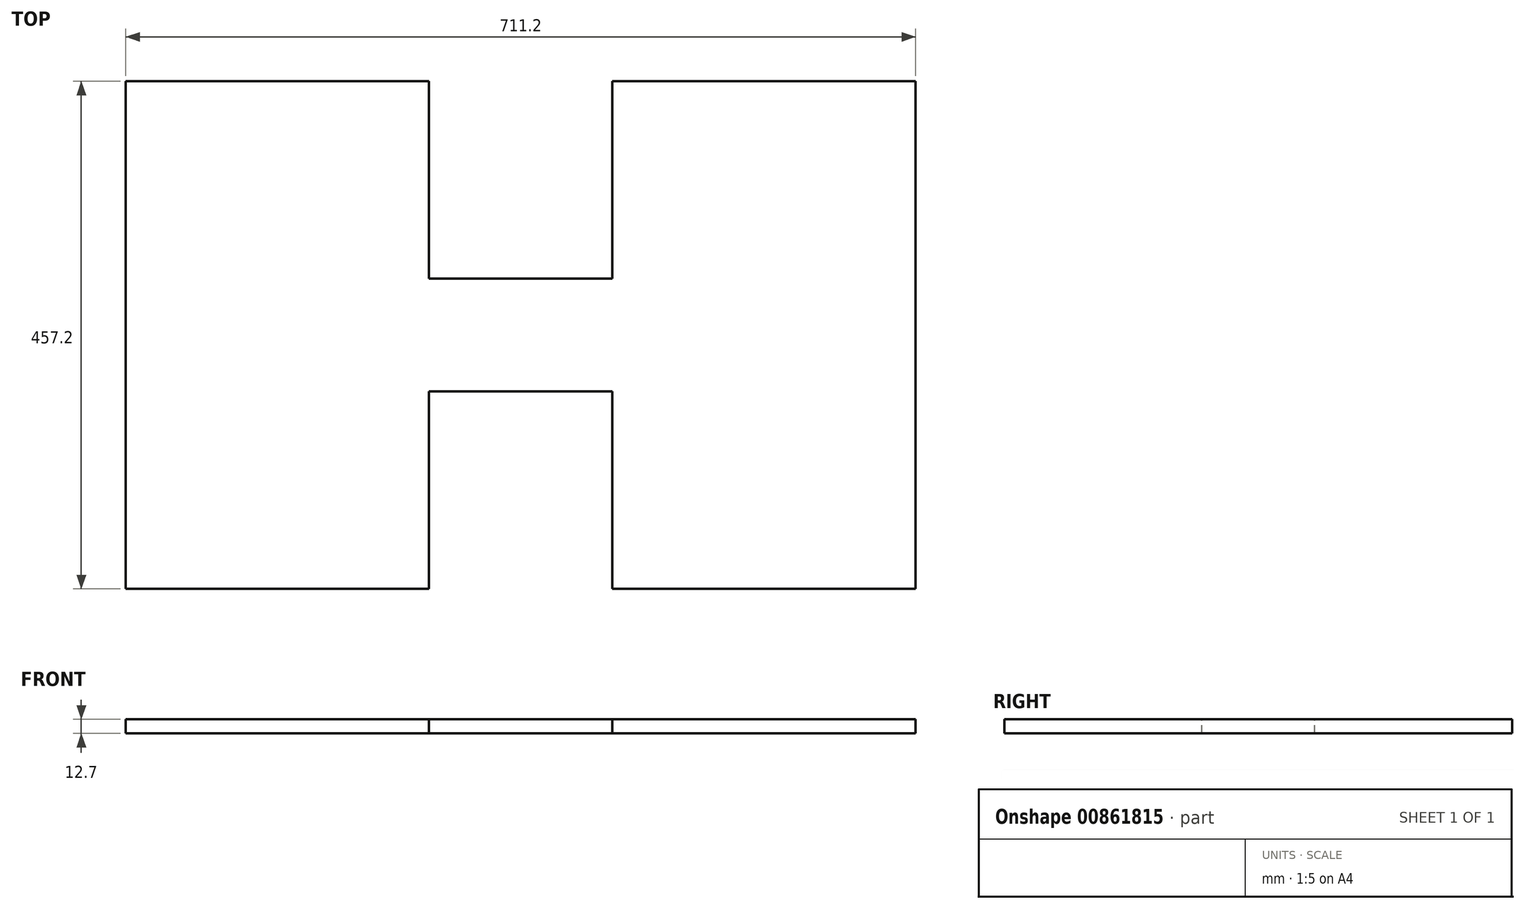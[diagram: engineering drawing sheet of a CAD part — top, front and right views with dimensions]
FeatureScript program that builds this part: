
annotation { "Feature Type Name" : "Feature", "Feature Type Description" : "" }
export const myFeature = defineFeature(function(context is Context, id is Id, definition is map)
    precondition{}
    {
        {
            var Q0;
            Q0=qCreatedBy(makeId("Top.planeOp"),FACE);
            var sketch = newSketch(context, id + "F0", { "sketchPlane" : qUnion([Q0])});
            skLineSegment(sketch, "E0.bottom", {"start": v(0, 0) * mm, "end": v(-711.2, 0) * mm});
            skLineSegment(sketch, "E0.top", {"start": v(0, 457.2) * mm, "end": v(-711.2, 457.2) * mm});
            skLineSegment(sketch, "E0.left", {"start": v(0, 0) * mm, "end": v(0, 457.2) * mm});
            skLineSegment(sketch, "E0.right", {"start": v(-711.2, 0) * mm, "end": v(-711.2, 457.2) * mm});
            skSolve(sketch);
        }
        {
            var Q0;
            Q0=makeQuery(id+"F0.imprint","IMPRINT",FACE,{"disambiguationData":[TD([[makeQuery(id+"F0.imprint","IMPRINT",EDGE,{"derivedFrom":sQuery(id+"F0.wireOp",EDGE,"E0.bottom")}),-1.0]])]});
            extrude(context, id + "F1", {"entities" : qUnion([Q0]), "depth" : 12.7 * mm, "offsetDistance" : 25.4 * mm});
        }
        {
            var Q0;
            Q0=makeQuery(id+"F1.opExtrude","CAP_FACE",FACE,{"disambiguationData":[OSD([sQuery(id+"F0.wireOp",EDGE,"E0.bottom"),sQuery(id+"F0.wireOp",EDGE,"E0.top"),sQuery(id+"F0.wireOp",EDGE,"E0.left"),sQuery(id+"F0.wireOp",EDGE,"E0.right")])],"isStart":false});
            var sketch = newSketch(context, id + "F2", { "sketchPlane" : qUnion([Q0])});
            skLineSegment(sketch, "E1.bottom", {"start": v(-273.05, 457.2) * mm, "end": v(-438.15, 457.2) * mm});
            skLineSegment(sketch, "E1.top", {"start": v(-273.05, 279.4) * mm, "end": v(-438.15, 279.4) * mm});
            skLineSegment(sketch, "E1.left", {"start": v(-273.05, 457.2) * mm, "end": v(-273.05, 279.4) * mm});
            skLineSegment(sketch, "E1.right", {"start": v(-438.15, 457.2) * mm, "end": v(-438.15, 279.4) * mm});
            skLineSegment(sketch, "E2.bottom", {"start": v(-438.15, 0) * mm, "end": v(-273.05, 0) * mm});
            skLineSegment(sketch, "E2.top", {"start": v(-438.15, 177.8) * mm, "end": v(-273.05, 177.8) * mm});
            skLineSegment(sketch, "E2.left", {"start": v(-438.15, 0) * mm, "end": v(-438.15, 177.8) * mm});
            skLineSegment(sketch, "E2.right", {"start": v(-273.05, 0) * mm, "end": v(-273.05, 177.8) * mm});
            skLineSegment(sketch, "E3", {"start": v(-273.05, 279.4) * mm, "end": v(-273.05, 177.8) * mm, "construction": true});
            skLineSegment(sketch, "E4", {"start": v(-438.15, 177.8) * mm, "end": v(-711.2, 177.8) * mm, "construction": true});
            skLineSegment(sketch, "E5", {"start": v(-273.05, 177.8) * mm, "end": v(0, 177.8) * mm, "construction": true});
            skSolve(sketch);
        }
        {
            var Q0;
            Q0=makeQuery(id+"F2.imprint","IMPRINT",FACE,{"disambiguationData":[TD([[makeQuery(id+"F2.imprint","IMPRINT",EDGE,{"derivedFrom":sQuery(id+"F2.wireOp",EDGE,"E1.bottom")}),1.0]])]});
            var Q1;
            Q1=makeQuery(id+"F2.imprint","IMPRINT",FACE,{"disambiguationData":[TD([[makeQuery(id+"F2.imprint","IMPRINT",EDGE,{"derivedFrom":sQuery(id+"F2.wireOp",EDGE,"E2.bottom")}),-1.0]])]});
            extrude(context, id + "F3", {"entities" : qUnion([Q0, Q1]), "operationType" : NewBodyOperationType.REMOVE, "oppositeDirection" : true, "depth" : 12.7 * mm, "offsetDistance" : 25.4 * mm});
        }
    });
